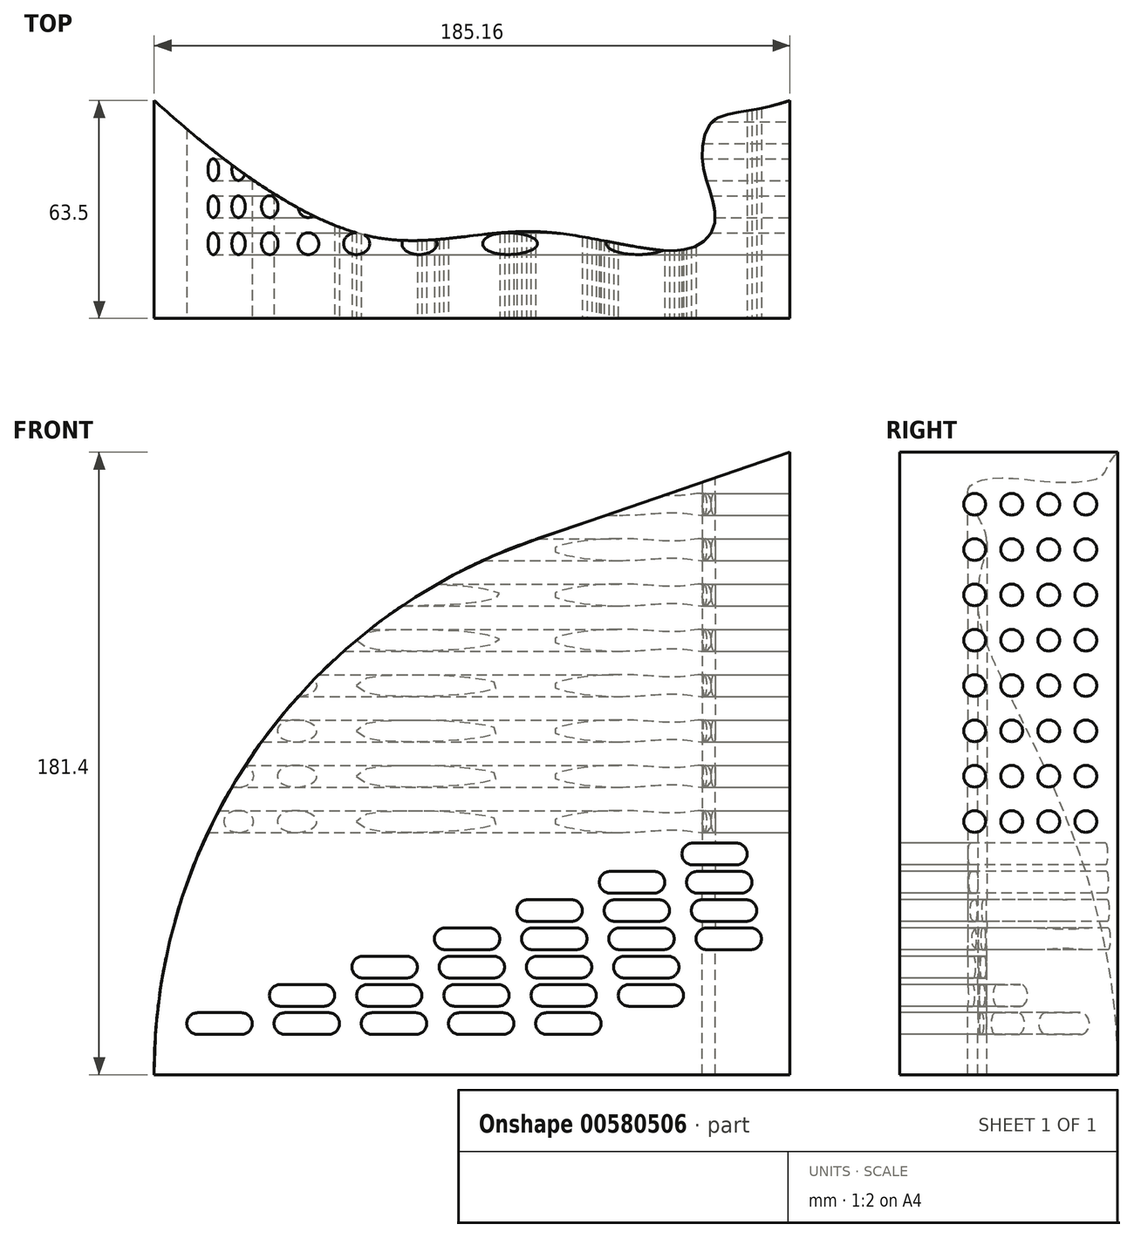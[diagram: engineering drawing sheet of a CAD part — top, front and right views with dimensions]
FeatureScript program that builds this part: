
annotation { "Feature Type Name" : "Feature", "Feature Type Description" : "" }
export const myFeature = defineFeature(function(context is Context, id is Id, definition is map)
    precondition{}
    {
        {
            var Q0;
            Q0=qCreatedBy(makeId("Front.planeOp"),FACE);
            var sketch = newSketch(context, id + "F0", { "sketchPlane" : qUnion([Q0])});
            skLineSegment(sketch, "E0", {"start": v(-138.31, 42.37) * mm, "end": v(46.85, 105.83) * mm});
            skLineSegment(sketch, "E1", {"start": v(-138.31, 42.37) * mm, "end": v(-138.31, -75.57) * mm});
            skLineSegment(sketch, "E2", {"start": v(-138.31, -75.57) * mm, "end": v(46.85, -75.57) * mm});
            skLineSegment(sketch, "E3", {"start": v(46.85, -75.57) * mm, "end": v(46.85, 105.83) * mm});
            skSolve(sketch);
        }
        {
            var Q0;
            Q0=makeQuery(id+"F0.imprint","IMPRINT",FACE,{"disambiguationData":[TD([[makeQuery(id+"F0.imprint","IMPRINT",EDGE,{"derivedFrom":sQuery(id+"F0.wireOp",EDGE,"E0")}),-1.0]])]});
            extrude(context, id + "F1", {"entities" : qUnion([Q0]), "depth" : 63.5 * mm, "offsetDistance" : 25.4 * mm});
        }
        {
            var Q0;
            Q0=makeQuery(id+"F1.opExtrude","CAP_FACE",FACE,{"disambiguationData":[OSD([sQuery(id+"F0.wireOp",EDGE,"E0"),sQuery(id+"F0.wireOp",EDGE,"E1"),sQuery(id+"F0.wireOp",EDGE,"E2"),sQuery(id+"F0.wireOp",EDGE,"E3")])],"isStart":false});
            var sketch = newSketch(context, id + "F2", { "sketchPlane" : qUnion([Q0])});
            skLineSegment(sketch, "E4.bottom", {"start": v(-125.61, -63.86) * mm, "end": v(-112.91, -63.86) * mm});
            skLineSegment(sketch, "E4.top", {"start": v(-125.61, -57.51) * mm, "end": v(-112.91, -57.51) * mm});
            skLineSegment(sketch, "E4.left", {"start": v(-125.61, -63.86) * mm, "end": v(-125.61, -57.51) * mm});
            skLineSegment(sketch, "E4.right", {"start": v(-112.91, -63.86) * mm, "end": v(-112.91, -57.51) * mm});
            skArc(sketch, "E5", {"start": v(-125.61, -57.51) * mm, "mid": v(-128.79, -60.69) * mm, "end": v(-125.61, -63.86) * mm});
            skArc(sketch, "E6", {"start": v(-112.91, -63.86) * mm, "mid": v(-109.74, -60.69) * mm, "end": v(-112.91, -57.51) * mm});
            skLineSegment(sketch, "E7.0.1.0", {"start": v(-101.58, -49.28) * mm, "end": v(-88.88, -49.28) * mm});
            skLineSegment(sketch, "E7.0.1.1", {"start": v(-101.58, -55.63) * mm, "end": v(-88.88, -55.63) * mm});
            skArc(sketch, "E7.0.1.2", {"start": v(-101.58, -49.28) * mm, "mid": v(-104.76, -52.45) * mm, "end": v(-101.58, -55.63) * mm});
            skArc(sketch, "E7.0.1.3", {"start": v(-88.88, -55.63) * mm, "mid": v(-85.7, -52.45) * mm, "end": v(-88.88, -49.28) * mm});
            skLineSegment(sketch, "E7.0.1.4", {"start": v(-88.88, -55.63) * mm, "end": v(-88.88, -49.28) * mm});
            skLineSegment(sketch, "E7.0.1.5", {"start": v(-101.58, -55.63) * mm, "end": v(-101.58, -49.28) * mm});
            skLineSegment(sketch, "E7.0.2.0", {"start": v(-77.56, -41.04) * mm, "end": v(-64.86, -41.04) * mm});
            skLineSegment(sketch, "E7.0.2.1", {"start": v(-77.56, -47.39) * mm, "end": v(-64.86, -47.39) * mm});
            skArc(sketch, "E7.0.2.2", {"start": v(-77.56, -41.04) * mm, "mid": v(-80.73, -44.21) * mm, "end": v(-77.56, -47.39) * mm});
            skArc(sketch, "E7.0.2.3", {"start": v(-64.86, -47.39) * mm, "mid": v(-61.68, -44.21) * mm, "end": v(-64.86, -41.04) * mm});
            skLineSegment(sketch, "E7.0.2.4", {"start": v(-64.86, -47.39) * mm, "end": v(-64.86, -41.04) * mm});
            skLineSegment(sketch, "E7.0.2.5", {"start": v(-77.56, -47.39) * mm, "end": v(-77.56, -41.04) * mm});
            skLineSegment(sketch, "E7.0.3.0", {"start": v(-53.53, -32.8) * mm, "end": v(-40.83, -32.8) * mm});
            skLineSegment(sketch, "E7.0.3.1", {"start": v(-53.53, -39.15) * mm, "end": v(-40.83, -39.15) * mm});
            skArc(sketch, "E7.0.3.2", {"start": v(-53.53, -32.8) * mm, "mid": v(-56.7, -35.98) * mm, "end": v(-53.53, -39.15) * mm});
            skArc(sketch, "E7.0.3.3", {"start": v(-40.83, -39.15) * mm, "mid": v(-37.65, -35.98) * mm, "end": v(-40.83, -32.8) * mm});
            skLineSegment(sketch, "E7.0.3.4", {"start": v(-40.83, -39.15) * mm, "end": v(-40.83, -32.8) * mm});
            skLineSegment(sketch, "E7.0.3.5", {"start": v(-53.53, -39.15) * mm, "end": v(-53.53, -32.8) * mm});
            skLineSegment(sketch, "E7.0.4.0", {"start": v(-29.5, -24.57) * mm, "end": v(-16.8, -24.57) * mm});
            skLineSegment(sketch, "E7.0.4.1", {"start": v(-29.5, -30.92) * mm, "end": v(-16.8, -30.92) * mm});
            skArc(sketch, "E7.0.4.2", {"start": v(-29.5, -24.57) * mm, "mid": v(-32.67, -27.74) * mm, "end": v(-29.5, -30.92) * mm});
            skArc(sketch, "E7.0.4.3", {"start": v(-16.8, -30.92) * mm, "mid": v(-13.62, -27.74) * mm, "end": v(-16.8, -24.57) * mm});
            skLineSegment(sketch, "E7.0.4.4", {"start": v(-16.8, -30.92) * mm, "end": v(-16.8, -24.57) * mm});
            skLineSegment(sketch, "E7.0.4.5", {"start": v(-29.5, -30.92) * mm, "end": v(-29.5, -24.57) * mm});
            skLineSegment(sketch, "E7.0.5.0", {"start": v(-5.47, -16.33) * mm, "end": v(7.23, -16.33) * mm});
            skLineSegment(sketch, "E7.0.5.1", {"start": v(-5.47, -22.68) * mm, "end": v(7.23, -22.68) * mm});
            skArc(sketch, "E7.0.5.2", {"start": v(-5.47, -16.33) * mm, "mid": v(-8.65, -19.5) * mm, "end": v(-5.47, -22.68) * mm});
            skArc(sketch, "E7.0.5.3", {"start": v(7.23, -22.68) * mm, "mid": v(10.4, -19.5) * mm, "end": v(7.23, -16.33) * mm});
            skLineSegment(sketch, "E7.0.5.4", {"start": v(7.23, -22.68) * mm, "end": v(7.23, -16.33) * mm});
            skLineSegment(sketch, "E7.0.5.5", {"start": v(-5.47, -22.68) * mm, "end": v(-5.47, -16.33) * mm});
            skLineSegment(sketch, "E7.0.6.0", {"start": v(18.56, -8.1) * mm, "end": v(31.26, -8.1) * mm});
            skLineSegment(sketch, "E7.0.6.1", {"start": v(18.56, -14.45) * mm, "end": v(31.26, -14.45) * mm});
            skArc(sketch, "E7.0.6.2", {"start": v(18.56, -8.1) * mm, "mid": v(15.38, -11.27) * mm, "end": v(18.56, -14.45) * mm});
            skArc(sketch, "E7.0.6.3", {"start": v(31.26, -14.45) * mm, "mid": v(34.43, -11.27) * mm, "end": v(31.26, -8.1) * mm});
            skLineSegment(sketch, "E7.0.6.4", {"start": v(31.26, -14.45) * mm, "end": v(31.26, -8.1) * mm});
            skLineSegment(sketch, "E7.0.6.5", {"start": v(18.56, -14.45) * mm, "end": v(18.56, -8.1) * mm});
            skLineSegment(sketch, "E7.1.0.0", {"start": v(-100.21, -57.51) * mm, "end": v(-87.51, -57.51) * mm});
            skLineSegment(sketch, "E7.1.0.1", {"start": v(-100.21, -63.86) * mm, "end": v(-87.51, -63.86) * mm});
            skArc(sketch, "E7.1.0.2", {"start": v(-100.21, -57.51) * mm, "mid": v(-103.39, -60.69) * mm, "end": v(-100.21, -63.86) * mm});
            skArc(sketch, "E7.1.0.3", {"start": v(-87.51, -63.86) * mm, "mid": v(-84.34, -60.69) * mm, "end": v(-87.51, -57.51) * mm});
            skLineSegment(sketch, "E7.1.0.4", {"start": v(-87.51, -63.86) * mm, "end": v(-87.51, -57.51) * mm});
            skLineSegment(sketch, "E7.1.0.5", {"start": v(-100.21, -63.86) * mm, "end": v(-100.21, -57.51) * mm});
            skLineSegment(sketch, "E7.1.1.0", {"start": v(-76.18, -49.28) * mm, "end": v(-63.48, -49.28) * mm});
            skLineSegment(sketch, "E7.1.1.1", {"start": v(-76.18, -55.63) * mm, "end": v(-63.48, -55.63) * mm});
            skArc(sketch, "E7.1.1.2", {"start": v(-76.18, -49.28) * mm, "mid": v(-79.36, -52.45) * mm, "end": v(-76.18, -55.63) * mm});
            skArc(sketch, "E7.1.1.3", {"start": v(-63.48, -55.63) * mm, "mid": v(-60.3, -52.45) * mm, "end": v(-63.48, -49.28) * mm});
            skLineSegment(sketch, "E7.1.1.4", {"start": v(-63.48, -55.63) * mm, "end": v(-63.48, -49.28) * mm});
            skLineSegment(sketch, "E7.1.1.5", {"start": v(-76.18, -55.63) * mm, "end": v(-76.18, -49.28) * mm});
            skLineSegment(sketch, "E7.1.2.0", {"start": v(-52.16, -41.04) * mm, "end": v(-39.46, -41.04) * mm});
            skLineSegment(sketch, "E7.1.2.1", {"start": v(-52.16, -47.39) * mm, "end": v(-39.46, -47.39) * mm});
            skArc(sketch, "E7.1.2.2", {"start": v(-52.16, -41.04) * mm, "mid": v(-55.33, -44.21) * mm, "end": v(-52.16, -47.39) * mm});
            skArc(sketch, "E7.1.2.3", {"start": v(-39.46, -47.39) * mm, "mid": v(-36.28, -44.21) * mm, "end": v(-39.46, -41.04) * mm});
            skLineSegment(sketch, "E7.1.2.4", {"start": v(-39.46, -47.39) * mm, "end": v(-39.46, -41.04) * mm});
            skLineSegment(sketch, "E7.1.2.5", {"start": v(-52.16, -47.39) * mm, "end": v(-52.16, -41.04) * mm});
            skLineSegment(sketch, "E7.1.3.0", {"start": v(-28.13, -32.8) * mm, "end": v(-15.43, -32.8) * mm});
            skLineSegment(sketch, "E7.1.3.1", {"start": v(-28.13, -39.15) * mm, "end": v(-15.43, -39.15) * mm});
            skArc(sketch, "E7.1.3.2", {"start": v(-28.13, -32.8) * mm, "mid": v(-31.3, -35.98) * mm, "end": v(-28.13, -39.15) * mm});
            skArc(sketch, "E7.1.3.3", {"start": v(-15.43, -39.15) * mm, "mid": v(-12.25, -35.98) * mm, "end": v(-15.43, -32.8) * mm});
            skLineSegment(sketch, "E7.1.3.4", {"start": v(-15.43, -39.15) * mm, "end": v(-15.43, -32.8) * mm});
            skLineSegment(sketch, "E7.1.3.5", {"start": v(-28.13, -39.15) * mm, "end": v(-28.13, -32.8) * mm});
            skLineSegment(sketch, "E7.1.4.0", {"start": v(-4.1, -24.57) * mm, "end": v(8.6, -24.57) * mm});
            skLineSegment(sketch, "E7.1.4.1", {"start": v(-4.1, -30.92) * mm, "end": v(8.6, -30.92) * mm});
            skArc(sketch, "E7.1.4.2", {"start": v(-4.1, -24.57) * mm, "mid": v(-7.27, -27.74) * mm, "end": v(-4.1, -30.92) * mm});
            skArc(sketch, "E7.1.4.3", {"start": v(8.6, -30.92) * mm, "mid": v(11.78, -27.74) * mm, "end": v(8.6, -24.57) * mm});
            skLineSegment(sketch, "E7.1.4.4", {"start": v(8.6, -30.92) * mm, "end": v(8.6, -24.57) * mm});
            skLineSegment(sketch, "E7.1.4.5", {"start": v(-4.1, -30.92) * mm, "end": v(-4.1, -24.57) * mm});
            skLineSegment(sketch, "E7.1.5.0", {"start": v(19.93, -16.33) * mm, "end": v(32.63, -16.33) * mm});
            skLineSegment(sketch, "E7.1.5.1", {"start": v(19.93, -22.68) * mm, "end": v(32.63, -22.68) * mm});
            skArc(sketch, "E7.1.5.2", {"start": v(19.93, -16.33) * mm, "mid": v(16.75, -19.5) * mm, "end": v(19.93, -22.68) * mm});
            skArc(sketch, "E7.1.5.3", {"start": v(32.63, -22.68) * mm, "mid": v(35.8, -19.5) * mm, "end": v(32.63, -16.33) * mm});
            skLineSegment(sketch, "E7.1.5.4", {"start": v(32.63, -22.68) * mm, "end": v(32.63, -16.33) * mm});
            skLineSegment(sketch, "E7.1.5.5", {"start": v(19.93, -22.68) * mm, "end": v(19.93, -16.33) * mm});
            skLineSegment(sketch, "E7.2.0.0", {"start": v(-74.81, -57.51) * mm, "end": v(-62.11, -57.51) * mm});
            skLineSegment(sketch, "E7.2.0.1", {"start": v(-74.81, -63.86) * mm, "end": v(-62.11, -63.86) * mm});
            skArc(sketch, "E7.2.0.2", {"start": v(-74.81, -57.51) * mm, "mid": v(-77.99, -60.69) * mm, "end": v(-74.81, -63.86) * mm});
            skArc(sketch, "E7.2.0.3", {"start": v(-62.11, -63.86) * mm, "mid": v(-58.94, -60.69) * mm, "end": v(-62.11, -57.51) * mm});
            skLineSegment(sketch, "E7.2.0.4", {"start": v(-62.11, -63.86) * mm, "end": v(-62.11, -57.51) * mm});
            skLineSegment(sketch, "E7.2.0.5", {"start": v(-74.81, -63.86) * mm, "end": v(-74.81, -57.51) * mm});
            skLineSegment(sketch, "E7.2.1.0", {"start": v(-50.78, -49.28) * mm, "end": v(-38.08, -49.28) * mm});
            skLineSegment(sketch, "E7.2.1.1", {"start": v(-50.78, -55.63) * mm, "end": v(-38.08, -55.63) * mm});
            skArc(sketch, "E7.2.1.2", {"start": v(-50.78, -49.28) * mm, "mid": v(-53.96, -52.45) * mm, "end": v(-50.78, -55.63) * mm});
            skArc(sketch, "E7.2.1.3", {"start": v(-38.08, -55.63) * mm, "mid": v(-34.9, -52.45) * mm, "end": v(-38.08, -49.28) * mm});
            skLineSegment(sketch, "E7.2.1.4", {"start": v(-38.08, -55.63) * mm, "end": v(-38.08, -49.28) * mm});
            skLineSegment(sketch, "E7.2.1.5", {"start": v(-50.78, -55.63) * mm, "end": v(-50.78, -49.28) * mm});
            skLineSegment(sketch, "E7.2.2.0", {"start": v(-26.76, -41.04) * mm, "end": v(-14.06, -41.04) * mm});
            skLineSegment(sketch, "E7.2.2.1", {"start": v(-26.76, -47.39) * mm, "end": v(-14.06, -47.39) * mm});
            skArc(sketch, "E7.2.2.2", {"start": v(-26.76, -41.04) * mm, "mid": v(-29.93, -44.21) * mm, "end": v(-26.76, -47.39) * mm});
            skArc(sketch, "E7.2.2.3", {"start": v(-14.06, -47.39) * mm, "mid": v(-10.88, -44.21) * mm, "end": v(-14.06, -41.04) * mm});
            skLineSegment(sketch, "E7.2.2.4", {"start": v(-14.06, -47.39) * mm, "end": v(-14.06, -41.04) * mm});
            skLineSegment(sketch, "E7.2.2.5", {"start": v(-26.76, -47.39) * mm, "end": v(-26.76, -41.04) * mm});
            skLineSegment(sketch, "E7.2.3.0", {"start": v(-2.73, -32.8) * mm, "end": v(9.97, -32.8) * mm});
            skLineSegment(sketch, "E7.2.3.1", {"start": v(-2.73, -39.15) * mm, "end": v(9.97, -39.15) * mm});
            skArc(sketch, "E7.2.3.2", {"start": v(-2.73, -32.8) * mm, "mid": v(-5.9, -35.98) * mm, "end": v(-2.73, -39.15) * mm});
            skArc(sketch, "E7.2.3.3", {"start": v(9.97, -39.15) * mm, "mid": v(13.15, -35.98) * mm, "end": v(9.97, -32.8) * mm});
            skLineSegment(sketch, "E7.2.3.4", {"start": v(9.97, -39.15) * mm, "end": v(9.97, -32.8) * mm});
            skLineSegment(sketch, "E7.2.3.5", {"start": v(-2.73, -39.15) * mm, "end": v(-2.73, -32.8) * mm});
            skLineSegment(sketch, "E7.2.4.0", {"start": v(21.3, -24.57) * mm, "end": v(34, -24.57) * mm});
            skLineSegment(sketch, "E7.2.4.1", {"start": v(21.3, -30.92) * mm, "end": v(34, -30.92) * mm});
            skArc(sketch, "E7.2.4.2", {"start": v(21.3, -24.57) * mm, "mid": v(18.13, -27.74) * mm, "end": v(21.3, -30.92) * mm});
            skArc(sketch, "E7.2.4.3", {"start": v(34, -30.92) * mm, "mid": v(37.18, -27.74) * mm, "end": v(34, -24.57) * mm});
            skLineSegment(sketch, "E7.2.4.4", {"start": v(34, -30.92) * mm, "end": v(34, -24.57) * mm});
            skLineSegment(sketch, "E7.2.4.5", {"start": v(21.3, -30.92) * mm, "end": v(21.3, -24.57) * mm});
            skLineSegment(sketch, "E7.3.0.0", {"start": v(-49.41, -57.51) * mm, "end": v(-36.71, -57.51) * mm});
            skLineSegment(sketch, "E7.3.0.1", {"start": v(-49.41, -63.86) * mm, "end": v(-36.71, -63.86) * mm});
            skArc(sketch, "E7.3.0.2", {"start": v(-49.41, -57.51) * mm, "mid": v(-52.59, -60.69) * mm, "end": v(-49.41, -63.86) * mm});
            skArc(sketch, "E7.3.0.3", {"start": v(-36.71, -63.86) * mm, "mid": v(-33.54, -60.69) * mm, "end": v(-36.71, -57.51) * mm});
            skLineSegment(sketch, "E7.3.0.4", {"start": v(-36.71, -63.86) * mm, "end": v(-36.71, -57.51) * mm});
            skLineSegment(sketch, "E7.3.0.5", {"start": v(-49.41, -63.86) * mm, "end": v(-49.41, -57.51) * mm});
            skLineSegment(sketch, "E7.3.1.0", {"start": v(-25.38, -49.28) * mm, "end": v(-12.68, -49.28) * mm});
            skLineSegment(sketch, "E7.3.1.1", {"start": v(-25.38, -55.63) * mm, "end": v(-12.68, -55.63) * mm});
            skArc(sketch, "E7.3.1.2", {"start": v(-25.38, -49.28) * mm, "mid": v(-28.56, -52.45) * mm, "end": v(-25.38, -55.63) * mm});
            skArc(sketch, "E7.3.1.3", {"start": v(-12.68, -55.63) * mm, "mid": v(-9.5, -52.45) * mm, "end": v(-12.68, -49.28) * mm});
            skLineSegment(sketch, "E7.3.1.4", {"start": v(-12.68, -55.63) * mm, "end": v(-12.68, -49.28) * mm});
            skLineSegment(sketch, "E7.3.1.5", {"start": v(-25.38, -55.63) * mm, "end": v(-25.38, -49.28) * mm});
            skLineSegment(sketch, "E7.3.2.0", {"start": v(-1.36, -41.04) * mm, "end": v(11.34, -41.04) * mm});
            skLineSegment(sketch, "E7.3.2.1", {"start": v(-1.36, -47.39) * mm, "end": v(11.34, -47.39) * mm});
            skArc(sketch, "E7.3.2.2", {"start": v(-1.36, -41.04) * mm, "mid": v(-4.53, -44.21) * mm, "end": v(-1.36, -47.39) * mm});
            skArc(sketch, "E7.3.2.3", {"start": v(11.34, -47.39) * mm, "mid": v(14.52, -44.21) * mm, "end": v(11.34, -41.04) * mm});
            skLineSegment(sketch, "E7.3.2.4", {"start": v(11.34, -47.39) * mm, "end": v(11.34, -41.04) * mm});
            skLineSegment(sketch, "E7.3.2.5", {"start": v(-1.36, -47.39) * mm, "end": v(-1.36, -41.04) * mm});
            skLineSegment(sketch, "E7.3.3.0", {"start": v(22.67, -32.8) * mm, "end": v(35.37, -32.8) * mm});
            skLineSegment(sketch, "E7.3.3.1", {"start": v(22.67, -39.15) * mm, "end": v(35.37, -39.15) * mm});
            skArc(sketch, "E7.3.3.2", {"start": v(22.67, -32.8) * mm, "mid": v(19.5, -35.98) * mm, "end": v(22.67, -39.15) * mm});
            skArc(sketch, "E7.3.3.3", {"start": v(35.37, -39.15) * mm, "mid": v(38.55, -35.98) * mm, "end": v(35.37, -32.8) * mm});
            skLineSegment(sketch, "E7.3.3.4", {"start": v(35.37, -39.15) * mm, "end": v(35.37, -32.8) * mm});
            skLineSegment(sketch, "E7.3.3.5", {"start": v(22.67, -39.15) * mm, "end": v(22.67, -32.8) * mm});
            skLineSegment(sketch, "E7.4.0.0", {"start": v(-24.01, -57.51) * mm, "end": v(-11.31, -57.51) * mm});
            skLineSegment(sketch, "E7.4.0.1", {"start": v(-24.01, -63.86) * mm, "end": v(-11.31, -63.86) * mm});
            skArc(sketch, "E7.4.0.2", {"start": v(-24.01, -57.51) * mm, "mid": v(-27.19, -60.69) * mm, "end": v(-24.01, -63.86) * mm});
            skArc(sketch, "E7.4.0.3", {"start": v(-11.31, -63.86) * mm, "mid": v(-8.14, -60.69) * mm, "end": v(-11.31, -57.51) * mm});
            skLineSegment(sketch, "E7.4.0.4", {"start": v(-11.31, -63.86) * mm, "end": v(-11.31, -57.51) * mm});
            skLineSegment(sketch, "E7.4.0.5", {"start": v(-24.01, -63.86) * mm, "end": v(-24.01, -57.51) * mm});
            skLineSegment(sketch, "E7.4.1.0", {"start": v(0.02, -49.28) * mm, "end": v(12.72, -49.28) * mm});
            skLineSegment(sketch, "E7.4.1.1", {"start": v(0.02, -55.63) * mm, "end": v(12.72, -55.63) * mm});
            skArc(sketch, "E7.4.1.2", {"start": v(0.02, -49.28) * mm, "mid": v(-3.16, -52.45) * mm, "end": v(0.02, -55.63) * mm});
            skArc(sketch, "E7.4.1.3", {"start": v(12.72, -55.63) * mm, "mid": v(15.9, -52.45) * mm, "end": v(12.72, -49.28) * mm});
            skLineSegment(sketch, "E7.4.1.4", {"start": v(12.72, -55.63) * mm, "end": v(12.72, -49.28) * mm});
            skLineSegment(sketch, "E7.4.1.5", {"start": v(0.02, -55.63) * mm, "end": v(0.02, -49.28) * mm});
            skLineSegment(sketch, "E7.direction1", {"start": v(-125.61, -63.86) * mm, "end": v(-100.21, -63.86) * mm, "construction": true});
            skLineSegment(sketch, "E7.direction2", {"start": v(-125.61, -63.86) * mm, "end": v(-101.58, -55.63) * mm, "construction": true});
            skSolve(sketch);
        }
        {
            var Q0;
            Q0 = qSketchRegion(id + "F2", true);
            extrude(context, id + "F3", {"entities" : qUnion([Q0]), "operationType" : NewBodyOperationType.REMOVE, "endBound" : BoundingType.THROUGH_ALL, "oppositeDirection" : true, "depth" : 25.4 * mm, "offsetDistance" : 25.4 * mm});
        }
        {
            var Q0;
            Q0=makeQuery(id+"F1.opExtrude","SWEPT_EDGE",EDGE,{"disambiguationData":[OSD([sQuery(id+"F0.wireOp",EDGE,"E0"),sQuery(id+"F0.wireOp",EDGE,"E1")])]});
            fillet(context, id + "F4", {"entities" : qUnion([Q0]), "radius" : 164.2 * mm, "tangentPropagation" : true, "allowEdgeOverflow" : false});
        }
        {
            var Q0;
            Q0=makeQuery(id+"F1.opExtrude","SWEPT_FACE",FACE,{"disambiguationData":[OSD([sQuery(id+"F0.wireOp",EDGE,"E2")])]});
            var sketch = newSketch(context, id + "F5", { "sketchPlane" : qUnion([Q0])});
            skLineSegment(sketch, "E8.0", {"start": v(-138.31, 63.5) * mm, "end": v(46.85, 63.5) * mm});
            skLineSegment(sketch, "E9.0.0", {"start": v(-138.31, 0) * mm, "end": v(46.85, 0) * mm});
            skLineSegment(sketch, "E9.0.1", {"start": v(46.85, 0) * mm, "end": v(46.85, 63.5) * mm});
            skLineSegment(sketch, "E9.0.2", {"start": v(46.85, 63.5) * mm, "end": v(-138.31, 63.5) * mm});
            skLineSegment(sketch, "E9.0.3", {"start": v(-138.31, 63.5) * mm, "end": v(-138.31, 0) * mm});
            skFitSpline(sketch, "E10", {"points": [v(46.85, 0) * mm, v(24.2, 6.19) * mm, v(21.57, 18.88) * mm, v(25.07, 34.84) * mm, v(16.95, 43.32) * mm, v(-26.03, 38.26) * mm, v(-74.25, 39.8) * mm, v(-138.31, 0) * mm, v(-165.7, -43.68) * mm, v(-41.87, -90) * mm, v(133.85, -66.5) * mm, v(46.85, 0) * mm]});
            skFitSpline(sketch, "E11.0", {"points": [v(51.16, 3.9) * mm, v(48.4, 4.85) * mm, v(45.8, 5.66) * mm, v(42.56, 6.55) * mm, v(38.93, 7.38) * mm, v(35.22, 8.05) * mm, v(32.2, 8.52) * mm, v(30.31, 8.86) * mm, v(29.2, 9.13) * mm, v(28.6, 9.33) * mm, v(28.2, 9.5) * mm, v(27.96, 9.64) * mm, v(27.85, 9.72) * mm, v(27.77, 9.8) * mm, v(27.67, 9.9) * mm, v(27.5, 10.12) * mm, v(27.2, 10.65) * mm, v(26.81, 11.65) * mm, v(26.47, 13.27) * mm, v(26.36, 14.86) * mm, v(26.38, 16.2) * mm, v(26.45, 17.06) * mm, v(26.53, 17.75) * mm, v(26.64, 18.44) * mm, v(26.8, 19.34) * mm, v(27.08, 20.47) * mm, v(27.51, 22.03) * mm, v(28.15, 24.1) * mm, v(28.97, 26.72) * mm, v(29.59, 29.03) * mm, v(29.96, 31) * mm, v(30.15, 32.53) * mm, v(30.2, 33.87) * mm, v(30.16, 34.98) * mm, v(30.06, 36.1) * mm, v(29.8, 37.49) * mm, v(29.3, 39.1) * mm, v(28.61, 40.66) * mm, v(27.43, 42.62) * mm, v(25.5, 44.78) * mm, v(23.04, 46.46) * mm, v(20.84, 47.47) * mm, v(19.08, 48.06) * mm, v(17.22, 48.47) * mm, v(15.34, 48.72) * mm, v(13.44, 48.82) * mm, v(10.85, 48.82) * mm, v(7.53, 48.57) * mm, v(3.4, 48) * mm, v(-0.89, 47.27) * mm, v(-5.28, 46.43) * mm, v(-9.76, 45.56) * mm, v(-14.27, 44.74) * mm, v(-18, 44.15) * mm, v(-20.96, 43.77) * mm, v(-23.15, 43.54) * mm, v(-25.3, 43.37) * mm, v(-27.4, 43.28) * mm, v(-29.5, 43.25) * mm, v(-32.3, 43.3) * mm, v(-35.8, 43.49) * mm, v(-40, 43.88) * mm, v(-45.68, 44.52) * mm, v(-52.9, 45.41) * mm, v(-60.41, 45.96) * mm, v(-66.66, 45.87) * mm, v(-70.66, 45.53) * mm, v(-73.92, 45.05) * mm, v(-77.21, 44.41) * mm, v(-81.34, 43.34) * mm, v(-86.3, 41.64) * mm, v(-92.92, 38.9) * mm, v(-101.17, 34.63) * mm, v(-111, 28.45) * mm, v(-120.7, 21.46) * mm, v(-128.58, 15.16) * mm, v(-134.73, 9.95) * mm, v(-139.25, 6) * mm, v(-143.67, 2.02) * mm, v(-147.99, -2) * mm, v(-152.14, -6.03) * mm, v(-157.36, -11.46) * mm, v(-162.01, -16.94) * mm, v(-165.84, -22.54) * mm, v(-168.23, -26.82) * mm, v(-170.05, -31.22) * mm, v(-171.18, -35.76) * mm, v(-171.42, -39.66) * mm, v(-171.12, -42.8) * mm, v(-170.62, -45.14) * mm, v(-169.87, -47.43) * mm, v(-168.55, -50.37) * mm, v(-166.34, -53.85) * mm, v(-162.94, -57.72) * mm, v(-158.86, -61.33) * mm, v(-154.13, -64.74) * mm, v(-147, -69.04) * mm, v(-136.58, -74.02) * mm, v(-121.88, -79.4) * mm, v(-105.16, -84.21) * mm, v(-86.65, -88.42) * mm, v(-66.57, -91.98) * mm, v(-45.14, -94.88) * mm, v(-22.59, -97.06) * mm, v(0.54, -98.49) * mm, v(23.64, -99.1) * mm, v(46.14, -98.87) * mm, v(67.46, -97.72) * mm, v(83.77, -95.95) * mm, v(95.67, -94.03) * mm, v(103.96, -92.3) * mm, v(111.56, -90.3) * mm, v(118.4, -87.97) * mm, v(124.45, -85.3) * mm, v(129.67, -82.18) * mm, v(133.27, -79.12) * mm, v(135.62, -76.3) * mm, v(137.07, -73.96) * mm, v(138.16, -71.43) * mm, v(138.7, -69.18) * mm, v(138.91, -67.34) * mm, v(138.96, -65.47) * mm, v(138.73, -63.15) * mm, v(138.07, -60.44) * mm, v(136.76, -56.9) * mm, v(134.4, -52.62) * mm, v(130.65, -47.55) * mm, v(126.08, -42.52) * mm, v(120.82, -37.52) * mm, v(114.96, -32.57) * mm, v(108.62, -27.7) * mm, v(99.67, -21.36) * mm, v(87.83, -13.86) * mm, v(75.89, -7.25) * mm, v(66.72, -2.68) * mm, v(60.15, 0.33) * mm, v(55.02, 2.46) * mm, v(51.16, 3.9) * mm, v(48.4, 4.85) * mm, v(45.8, 5.66) * mm, v(51.16, 3.9) * mm]});
            skSolve(sketch);
        }
        {
            var Q0;
            {var subQ0=sQuery(id+"F5.wireOp",EDGE,"E9.0.0");Q0=makeQuery(id+"F5.imprint","IMPRINT",FACE,{"disambiguationData":[TD([[makeQuery(id+"F5.imprint","IMPRINT",EDGE,{"derivedFrom":subQ0}),1.0]])]});}
            var Q1;
            {var subQ0=sQuery(id+"F5.wireOp",EDGE,"E9.0.2");Q1=makeQuery(id+"F5.imprint","IMPRINT",FACE,{"disambiguationData":[TD([[makeQuery(id+"F5.imprint","IMPRINT",EDGE,{"derivedFrom":subQ0}),-1.0]])]});}
            extrude(context, id + "F6", {"entities" : qUnion([Q0, Q1]), "operationType" : NewBodyOperationType.REMOVE, "endBound" : BoundingType.THROUGH_ALL, "oppositeDirection" : true, "depth" : 25.4 * mm, "offsetDistance" : 25.4 * mm});
        }
        {
            var Q0;
            Q0=makeQuery(id+"F1.opExtrude","SWEPT_FACE",FACE,{"disambiguationData":[OSD([sQuery(id+"F0.wireOp",EDGE,"E3")])]});
            var sketch = newSketch(context, id + "F7", { "sketchPlane" : qUnion([Q0])});
            skCircle(sketch, "E12", {"center": v(-41.72, 90.67) * mm, "radius": 3.18 * mm});
            skCircle(sketch, "E13.0.1.0", {"center": v(-41.72, 77.46) * mm, "radius": 3.18 * mm});
            skCircle(sketch, "E13.0.2.0", {"center": v(-41.72, 64.25) * mm, "radius": 3.18 * mm});
            skCircle(sketch, "E13.0.3.0", {"center": v(-41.72, 51.04) * mm, "radius": 3.18 * mm});
            skCircle(sketch, "E13.0.4.0", {"center": v(-41.72, 37.84) * mm, "radius": 3.18 * mm});
            skCircle(sketch, "E13.0.5.0", {"center": v(-41.72, 24.63) * mm, "radius": 3.18 * mm});
            skCircle(sketch, "E13.0.6.0", {"center": v(-41.72, 11.42) * mm, "radius": 3.18 * mm});
            skCircle(sketch, "E13.0.7.0", {"center": v(-41.72, -1.79) * mm, "radius": 3.18 * mm});
            skCircle(sketch, "E13.1.0.0", {"center": v(-30.93, 90.67) * mm, "radius": 3.18 * mm});
            skCircle(sketch, "E13.1.1.0", {"center": v(-30.93, 77.46) * mm, "radius": 3.18 * mm});
            skCircle(sketch, "E13.1.2.0", {"center": v(-30.93, 64.25) * mm, "radius": 3.18 * mm});
            skCircle(sketch, "E13.1.3.0", {"center": v(-30.93, 51.04) * mm, "radius": 3.18 * mm});
            skCircle(sketch, "E13.1.4.0", {"center": v(-30.93, 37.84) * mm, "radius": 3.18 * mm});
            skCircle(sketch, "E13.1.5.0", {"center": v(-30.93, 24.63) * mm, "radius": 3.18 * mm});
            skCircle(sketch, "E13.1.6.0", {"center": v(-30.93, 11.42) * mm, "radius": 3.18 * mm});
            skCircle(sketch, "E13.1.7.0", {"center": v(-30.93, -1.79) * mm, "radius": 3.18 * mm});
            skCircle(sketch, "E13.2.0.0", {"center": v(-20.13, 90.67) * mm, "radius": 3.18 * mm});
            skCircle(sketch, "E13.2.1.0", {"center": v(-20.13, 77.46) * mm, "radius": 3.18 * mm});
            skCircle(sketch, "E13.2.2.0", {"center": v(-20.13, 64.25) * mm, "radius": 3.18 * mm});
            skCircle(sketch, "E13.2.3.0", {"center": v(-20.13, 51.04) * mm, "radius": 3.18 * mm});
            skCircle(sketch, "E13.2.4.0", {"center": v(-20.13, 37.84) * mm, "radius": 3.18 * mm});
            skCircle(sketch, "E13.2.5.0", {"center": v(-20.13, 24.63) * mm, "radius": 3.18 * mm});
            skCircle(sketch, "E13.2.6.0", {"center": v(-20.13, 11.42) * mm, "radius": 3.18 * mm});
            skCircle(sketch, "E13.2.7.0", {"center": v(-20.13, -1.79) * mm, "radius": 3.18 * mm});
            skCircle(sketch, "E13.3.0.0", {"center": v(-9.34, 90.67) * mm, "radius": 3.18 * mm});
            skCircle(sketch, "E13.3.1.0", {"center": v(-9.34, 77.46) * mm, "radius": 3.18 * mm});
            skCircle(sketch, "E13.3.2.0", {"center": v(-9.34, 64.25) * mm, "radius": 3.18 * mm});
            skCircle(sketch, "E13.3.3.0", {"center": v(-9.34, 51.04) * mm, "radius": 3.18 * mm});
            skCircle(sketch, "E13.3.4.0", {"center": v(-9.34, 37.84) * mm, "radius": 3.18 * mm});
            skCircle(sketch, "E13.3.5.0", {"center": v(-9.34, 24.63) * mm, "radius": 3.18 * mm});
            skCircle(sketch, "E13.3.6.0", {"center": v(-9.34, 11.42) * mm, "radius": 3.18 * mm});
            skCircle(sketch, "E13.3.7.0", {"center": v(-9.34, -1.79) * mm, "radius": 3.18 * mm});
            skLineSegment(sketch, "E13.direction1", {"start": v(-41.72, 90.67) * mm, "end": v(-30.93, 90.67) * mm, "construction": true});
            skLineSegment(sketch, "E13.direction2", {"start": v(-41.72, 90.67) * mm, "end": v(-41.72, 77.46) * mm, "construction": true});
            skSolve(sketch);
        }
        {
            var Q0;
            Q0 = qSketchRegion(id + "F7", true);
            extrude(context, id + "F8", {"entities" : qUnion([Q0]), "operationType" : NewBodyOperationType.REMOVE, "endBound" : BoundingType.THROUGH_ALL, "oppositeDirection" : true, "depth" : 25.4 * mm, "offsetDistance" : 25.4 * mm});
        }
    });
